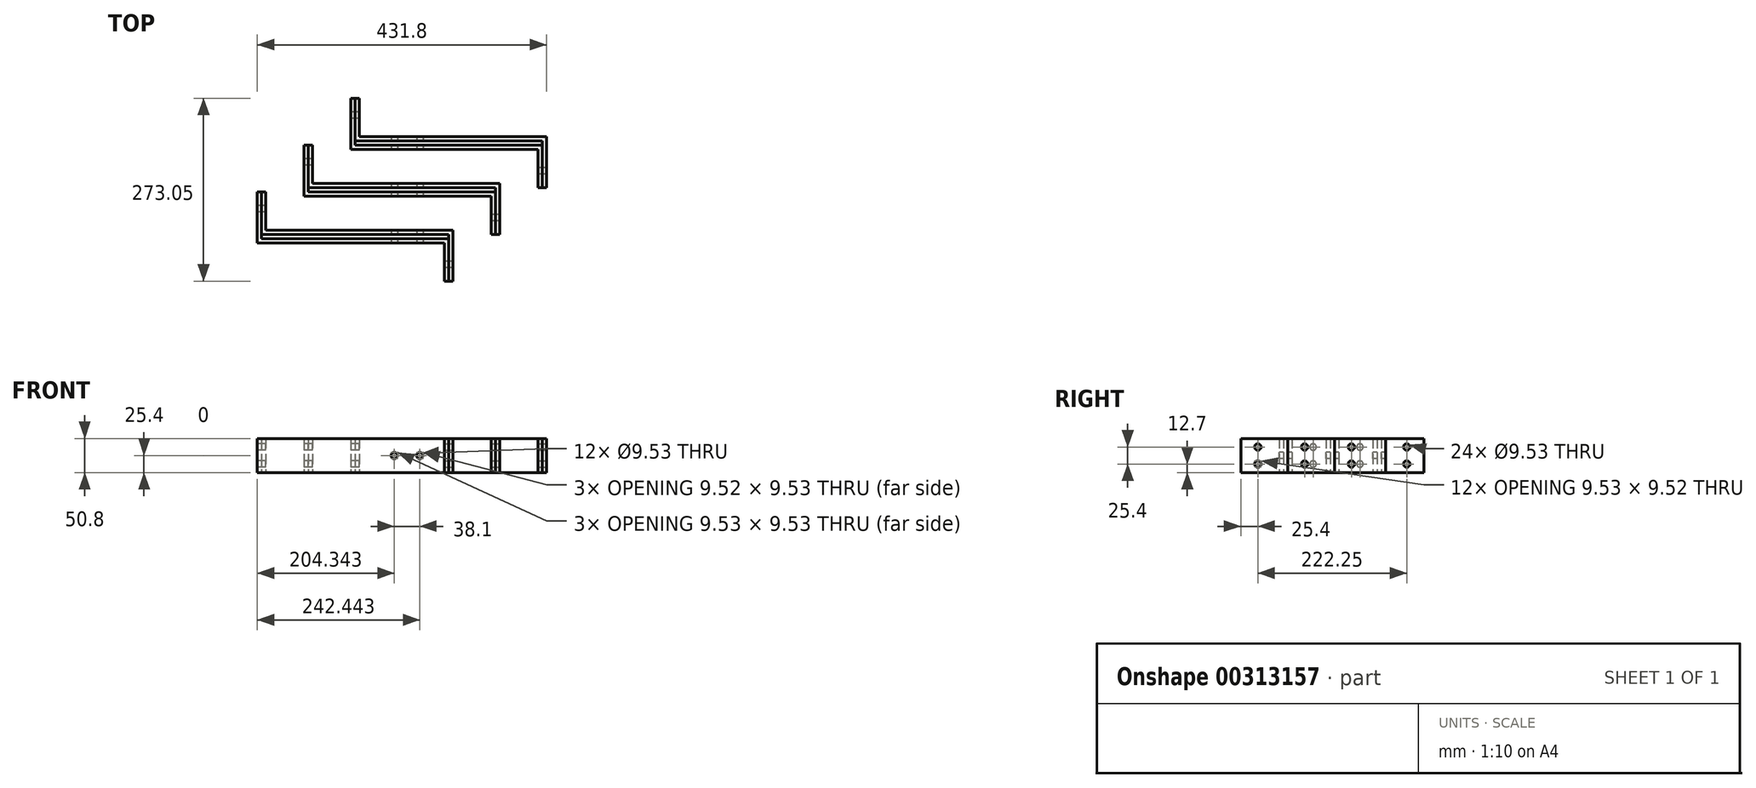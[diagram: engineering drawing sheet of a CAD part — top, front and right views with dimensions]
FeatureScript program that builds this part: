
annotation { "Feature Type Name" : "Feature", "Feature Type Description" : "" }
export const myFeature = defineFeature(function(context is Context, id is Id, definition is map)
    precondition{}
    {
        {
            var Q0;
            Q0=qCreatedBy(makeId("Top.planeOp"),FACE);
            var sketch = newSketch(context, id + "F0", { "sketchPlane" : qUnion([Q0])});
            skLineSegment(sketch, "E0", {"start": v(-279.4, 133.35) * mm, "end": v(-279.4, 63.5) * mm});
            skLineSegment(sketch, "E1", {"start": v(-279.4, 63.5) * mm, "end": v(0, 63.5) * mm});
            skLineSegment(sketch, "E2", {"start": v(0, 63.5) * mm, "end": v(0, 0) * mm});
            skLineSegment(sketch, "E3", {"start": v(0, 0) * mm, "end": v(-6.35, 0) * mm});
            skLineSegment(sketch, "E4", {"start": v(-6.35, 0) * mm, "end": v(-6.35, 57.15) * mm});
            skLineSegment(sketch, "E5", {"start": v(-6.35, 57.15) * mm, "end": v(-285.75, 57.15) * mm});
            skLineSegment(sketch, "E6", {"start": v(-285.75, 57.15) * mm, "end": v(-285.75, 133.35) * mm});
            skLineSegment(sketch, "E7", {"start": v(-285.75, 133.35) * mm, "end": v(-279.4, 133.35) * mm});
            skLineSegment(sketch, "E8", {"start": v(-209.55, 203.2) * mm, "end": v(-209.55, 133.35) * mm});
            skLineSegment(sketch, "E9", {"start": v(-209.55, 133.35) * mm, "end": v(69.85, 133.35) * mm});
            skLineSegment(sketch, "E10", {"start": v(69.85, 133.35) * mm, "end": v(69.85, 69.85) * mm});
            skLineSegment(sketch, "E11", {"start": v(69.85, 69.85) * mm, "end": v(63.5, 69.85) * mm});
            skLineSegment(sketch, "E12", {"start": v(63.5, 69.85) * mm, "end": v(63.5, 127) * mm});
            skLineSegment(sketch, "E13", {"start": v(63.5, 127) * mm, "end": v(-215.9, 127) * mm});
            skLineSegment(sketch, "E14", {"start": v(-215.9, 127) * mm, "end": v(-215.9, 203.2) * mm});
            skLineSegment(sketch, "E15", {"start": v(-215.9, 203.2) * mm, "end": v(-209.55, 203.2) * mm});
            skLineSegment(sketch, "E16", {"start": v(-139.7, 273.05) * mm, "end": v(-139.7, 203.2) * mm});
            skLineSegment(sketch, "E17", {"start": v(-139.7, 203.2) * mm, "end": v(139.7, 203.2) * mm});
            skLineSegment(sketch, "E18", {"start": v(139.7, 203.2) * mm, "end": v(139.7, 139.7) * mm});
            skLineSegment(sketch, "E19", {"start": v(139.7, 139.7) * mm, "end": v(133.35, 139.7) * mm});
            skLineSegment(sketch, "E20", {"start": v(133.35, 139.7) * mm, "end": v(133.35, 196.85) * mm});
            skLineSegment(sketch, "E21", {"start": v(133.35, 196.85) * mm, "end": v(-146.05, 196.85) * mm});
            skLineSegment(sketch, "E22", {"start": v(-146.05, 196.85) * mm, "end": v(-146.05, 273.05) * mm});
            skLineSegment(sketch, "E23", {"start": v(-146.05, 273.05) * mm, "end": v(-139.7, 273.05) * mm});
            skSolve(sketch);
        }
        {
            var Q0;
            Q0=qSketchRegion(id+"F0",true);
            extrude(context, id + "F1", {"entities" : qUnion([Q0]), "endBound" : BoundingType.SYMMETRIC, "depth" : 50.8 * mm});
        }
        {
            var Q0;
            Q0=qCreatedBy(makeId("Top.planeOp"),FACE);
            var sketch = newSketch(context, id + "F2", { "sketchPlane" : qUnion([Q0])});
            skLineSegment(sketch, "E24", {"start": v(-273.05, 133.35) * mm, "end": v(-273.05, 76.2) * mm});
            skLineSegment(sketch, "E25", {"start": v(-273.05, 76.2) * mm, "end": v(6.35, 76.2) * mm});
            skLineSegment(sketch, "E26", {"start": v(6.35, 76.2) * mm, "end": v(6.35, 0) * mm});
            skLineSegment(sketch, "E27", {"start": v(6.35, 0) * mm, "end": v(0, 0) * mm});
            skLineSegment(sketch, "E28", {"start": v(0, 0) * mm, "end": v(0, 69.85) * mm});
            skLineSegment(sketch, "E29", {"start": v(0, 69.85) * mm, "end": v(-279.4, 69.85) * mm});
            skLineSegment(sketch, "E30", {"start": v(-279.4, 69.85) * mm, "end": v(-279.4, 133.35) * mm});
            skLineSegment(sketch, "E31", {"start": v(-279.4, 133.35) * mm, "end": v(-273.05, 133.35) * mm});
            skLineSegment(sketch, "E32", {"start": v(-203.2, 203.2) * mm, "end": v(-203.2, 146.05) * mm});
            skLineSegment(sketch, "E33", {"start": v(-203.2, 146.05) * mm, "end": v(76.2, 146.05) * mm});
            skLineSegment(sketch, "E34", {"start": v(76.2, 146.05) * mm, "end": v(76.2, 69.85) * mm});
            skLineSegment(sketch, "E35", {"start": v(76.2, 69.85) * mm, "end": v(69.85, 69.85) * mm});
            skLineSegment(sketch, "E36", {"start": v(69.85, 69.85) * mm, "end": v(69.85, 139.7) * mm});
            skLineSegment(sketch, "E37", {"start": v(69.85, 139.7) * mm, "end": v(-209.55, 139.7) * mm});
            skLineSegment(sketch, "E38", {"start": v(-209.55, 139.7) * mm, "end": v(-209.55, 203.2) * mm});
            skLineSegment(sketch, "E39", {"start": v(-209.55, 203.2) * mm, "end": v(-203.2, 203.2) * mm});
            skLineSegment(sketch, "E40", {"start": v(-133.35, 273.05) * mm, "end": v(-133.35, 215.9) * mm});
            skLineSegment(sketch, "E41", {"start": v(-133.35, 215.9) * mm, "end": v(146.05, 215.9) * mm});
            skLineSegment(sketch, "E42", {"start": v(146.05, 215.9) * mm, "end": v(146.05, 139.7) * mm});
            skLineSegment(sketch, "E43", {"start": v(146.05, 139.7) * mm, "end": v(139.7, 139.7) * mm});
            skLineSegment(sketch, "E44", {"start": v(139.7, 139.7) * mm, "end": v(139.7, 209.55) * mm});
            skLineSegment(sketch, "E45", {"start": v(139.7, 209.55) * mm, "end": v(-139.7, 209.55) * mm});
            skLineSegment(sketch, "E46", {"start": v(-139.7, 209.55) * mm, "end": v(-139.7, 273.05) * mm});
            skLineSegment(sketch, "E47", {"start": v(-139.7, 273.05) * mm, "end": v(-133.35, 273.05) * mm});
            skSolve(sketch);
        }
        {
            var Q0;
            Q0 = qSketchRegion(id + "F2", true);
            extrude(context, id + "F3", {"entities" : qUnion([Q0]), "endBound" : BoundingType.SYMMETRIC, "depth" : 50.8 * mm});
        }
        {
            var Q0;
            Q0=makeQuery(id+"F1.opExtrude","SWEPT_FACE",FACE,{"disambiguationData":[OSD([sQuery(id+"F0.wireOp",EDGE,"E5")])]});
            var sketch = newSketch(context, id + "F4", { "sketchPlane" : qUnion([Q0])});
            skCircle(sketch, "E48", {"center": v(-43.3, 0) * mm, "radius": 4.76 * mm});
            skCircle(sketch, "E49", {"center": v(-81.4, 0) * mm, "radius": 4.76 * mm});
            skPoint(sketch, "E50", {"position": v(-6.35, 0) * mm});
            skSolve(sketch);
        }
        {
            var Q0;
            Q0=qSketchRegion(id+"F4",true);
            var Q1;
            Q1=makeQuery(id+"F3.opExtrude","SWEPT_FACE",FACE,{"disambiguationData":[OSD([sQuery(id+"F2.wireOp",EDGE,"E25")])]});
            extrude(context, id + "F5", {"entities" : qUnion([Q0]), "operationType" : NewBodyOperationType.REMOVE, "endBound" : BoundingType.THROUGH_ALL, "oppositeDirection" : true, "endBoundEntityFace" : qUnion([Q1]), "depth" : 25.4 * mm});
        }
        {
            var Q0;
            Q0=makeQuery(id+"F1.opExtrude","SWEPT_FACE",FACE,{"disambiguationData":[OSD([sQuery(id+"F0.wireOp",EDGE,"E6")])]});
            var sketch = newSketch(context, id + "F6", { "sketchPlane" : qUnion([Q0])});
            skCircle(sketch, "E51", {"center": v(-107.95, 12.7) * mm, "radius": 4.76 * mm});
            skCircle(sketch, "E52", {"center": v(-107.95, -12.7) * mm, "radius": 4.76 * mm});
            skCircle(sketch, "E53.1.0.0", {"center": v(-177.8, 12.7) * mm, "radius": 4.76 * mm});
            skCircle(sketch, "E53.1.0.1", {"center": v(-177.8, -12.7) * mm, "radius": 4.76 * mm});
            skCircle(sketch, "E53.2.0.0", {"center": v(-247.65, 12.7) * mm, "radius": 4.76 * mm});
            skCircle(sketch, "E53.2.0.1", {"center": v(-247.65, -12.7) * mm, "radius": 4.76 * mm});
            skLineSegment(sketch, "E53.direction1", {"start": v(-107.95, -12.7) * mm, "end": v(-177.8, -12.7) * mm, "construction": true});
            skSolve(sketch);
        }
        {
            var Q0;
            Q0 = qSketchRegion(id + "F6", true);
            var Q1;
            Q1=makeQuery(id+"F3.opExtrude","SWEPT_FACE",FACE,{"disambiguationData":[OSD([sQuery(id+"F2.wireOp",EDGE,"E40")])]});
            extrude(context, id + "F7", {"entities" : qUnion([Q0]), "operationType" : NewBodyOperationType.REMOVE, "endBound" : BoundingType.UP_TO_SURFACE, "oppositeDirection" : true, "endBoundEntityFace" : qUnion([Q1]), "depth" : 25.4 * mm});
        }
        {
            var Q0;
            Q0=makeQuery(id+"F3.opExtrude","SWEPT_FACE",FACE,{"disambiguationData":[OSD([sQuery(id+"F2.wireOp",EDGE,"E42")])]});
            var sketch = newSketch(context, id + "F8", { "sketchPlane" : qUnion([Q0])});
            skCircle(sketch, "E54", {"center": v(165.1, 12.7) * mm, "radius": 4.76 * mm});
            skCircle(sketch, "E55", {"center": v(165.1, -12.7) * mm, "radius": 4.76 * mm});
            skCircle(sketch, "E56.1.0.0", {"center": v(95.25, 12.7) * mm, "radius": 4.76 * mm});
            skCircle(sketch, "E56.1.0.1", {"center": v(95.25, -12.7) * mm, "radius": 4.76 * mm});
            skCircle(sketch, "E56.2.0.0", {"center": v(25.4, 12.7) * mm, "radius": 4.76 * mm});
            skCircle(sketch, "E56.2.0.1", {"center": v(25.4, -12.7) * mm, "radius": 4.76 * mm});
            skLineSegment(sketch, "E56.direction1", {"start": v(165.1, -12.7) * mm, "end": v(95.25, -12.7) * mm, "construction": true});
            skSolve(sketch);
        }
        {
            var Q0;
            Q0 = qSketchRegion(id + "F8", true);
            var Q1;
            Q1=makeQuery(id+"F1.opExtrude","SWEPT_FACE",FACE,{"disambiguationData":[OSD([sQuery(id+"F0.wireOp",EDGE,"E4")])]});
            extrude(context, id + "F9", {"entities" : qUnion([Q0]), "operationType" : NewBodyOperationType.REMOVE, "endBound" : BoundingType.UP_TO_SURFACE, "oppositeDirection" : true, "endBoundEntityFace" : qUnion([Q1]), "depth" : 25.4 * mm});
        }
    });
